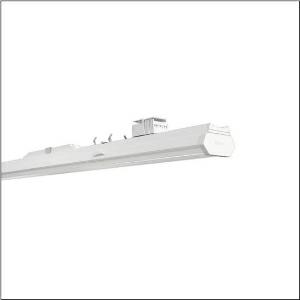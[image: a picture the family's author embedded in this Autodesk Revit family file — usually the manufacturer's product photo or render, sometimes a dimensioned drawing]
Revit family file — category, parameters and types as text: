
# Revit family: licross_r__21_protected_ho_52tp12dn4e5m3s_60f2
name_source: partatom
category: Lighting Fixtures
units: mm (PartAtom-declared; Revit-internal decimal feet)

## family parameters
Cut with Voids When Loaded = No
Host = Face
Light Source = No
Part Type = Normal
Room Calculation Point = No
Round Connector Dimension = Use Diameter
Shared = No

## types (1)
- --- (1 x LED, 910 lm, 7.6 W, 4000K)
    Apparent Load = 8 VA
    CIE Flux Codes = 70 91 97 98 100
    Color Rendering = 80
    Color Temperature = 4000K
    Default Elevation = 1800 mm
    Description = Licross® 21 Protected HO, luminaire insert, of sheet steel, galvanised, coil coated, white, length: 1.500mm, width: 90mm, height: 103mm, LED rated luminous flux: 14.690lm, light colour: 840, control gear: DALI 2 (for two DALI lines), with plug, 6-pole, with phase selection, for trunking rail, 14-core, mains connection: 220..240V, AC, 50/60Hz, rated input power: 89W, for trunking rail, 14-core, halogen-free wiring, for emergency light function, converter,control gear: single battery element, battery: LiFePO4, 9Ah, primary light control with lens, of plastic, primary optical cover: cover, of PMMA, light emission: direct distribution, primary light characteristic: symmetric, protection rating (complete): IP64, insulation class (complete): insulation class I (protective earthing), certification: CE, UKCA, protection symbol: D if used in an environment with conductive dust loads with corresponding accessories, impact resistance: IK06, permissible ambient temperature for indoor applications: +5..+30°C, standard: EN 60598-2-22, LABS conformity tested according to VDMA 24364:2018-05, reducing of maximum allowable ambient temperature of 5°C with ceiling mounting, corresponds to IFS (International Featured Standards) requirements for safety and quality in the food industry, packaging unit: 1 piece
    Height = 92 mm
    Lamp = 1 x LED
    Lamp Light Flux = 910 lm
    Lamp Power = 7.6 W
    Lamp count = 1
    Length = 1500 mm
    Luminous efficacy = 120 lm/W
    Manufacturer = Siteco
    ModVariant = No
    Model = 52TP12DN4E5M3S
    Mounting Place = Ceiling
    Mounting Type = Pendant
    Number of Poles = 1
    OnlyDefault = Yes
    Power Factor = 1
    Product Name = Licross® 21 Protected HO
    Product group = luminaire insert
    ProductGroupID = 902
    Protection Class = Protection class I
    Protection Degree = IP 64
    RLX_Detail_Level = 1
    RLX_Emergency_Light_Flux = 0 lm
    RLX_Emergency_Type = 0
    RLX_Emergency_Type_DB = No
    RlxData = <blob elided: 24949 chars, md5=08c46845>
    Socket = socket
    Standby Power = 0 W
    System Light Flux = 910 lm
    System Power = 8 W
    Type Comments = : emergency light operation: 3 h
    Type Image = l_1256148.jpg
    URL = http://relux.com
    VarID = @adj_111230
    Voltage = 0 V
    Weight = 0.00 kg
    Width = 88 mm

## geometry (parser evidence)
native form markers: Blend x4, Sweep x12
no freeform markers — native parametric forms only
